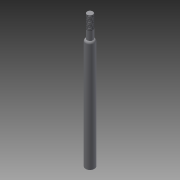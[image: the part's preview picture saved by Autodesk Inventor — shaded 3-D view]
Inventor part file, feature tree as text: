
AUTODESK INVENTOR PART (.ipt)
format: ipt  version: 2015 (Build 190159000, 159)  size: 84,992 bytes
history: native  units: mm
features: extrude x2, fillet x2, sketch x2, thread x1, chamfer x1
ambient origin geometry x8: Origin, YZ Plane, XZ Plane, XY Plane, X Axis, Y Axis, Z Axis, Center Point
bodies: Solid1 (feature_tree)
feature tree (8):
  extrude  "Extrusion1"  Depth=90.0mm TaperAngle=0.0deg
  extrude  "Extrusion2"  Depth=2.0mm TaperAngle=0.0deg
  thread  "Thread1"  [1 undecoded]
  fillet  "Fillet1"  Radius=0.25mm
  fillet  "Fillet2"  Radius=1.5mm
  chamfer  "Chamfer1"  Distance=2.0mm Angle=45.0deg
  sketch  "Sketch1"  dims[d0=6.0mm d1=90.0mm d2=0.0mm]
  sketch  "Sketch2"  dims[d3=4.0mm d4=15.0mm d5=0.0mm d6=10.0mm d7=6.0mm d8=0.25mm d9=1.5mm d10=0.5mm d11=2.0mm d12=45.0deg]
note: 1 required parameter value undecoded (feature->parameter linkage not recoverable at this tier; creation-order binding heuristic only, values carry confidence <= 0.55)
